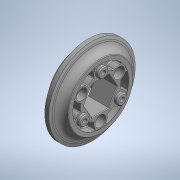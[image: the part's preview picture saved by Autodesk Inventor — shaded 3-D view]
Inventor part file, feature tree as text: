
AUTODESK INVENTOR PART (.ipt)
format: ipt  version: 2020 (Build 240168000, 168)  size: 552,448 bytes
history: native  units: mm (DEFAULTED — no unit token found)
features: mirror x1
ambient origin geometry x8: Origin, YZ Plane, XZ Plane, XY Plane, X Axis, Y Axis, Z Axis, Center Point
bodies: Solid1 (feature_tree)
feature tree (1):
  mirror  "Mirror2"
